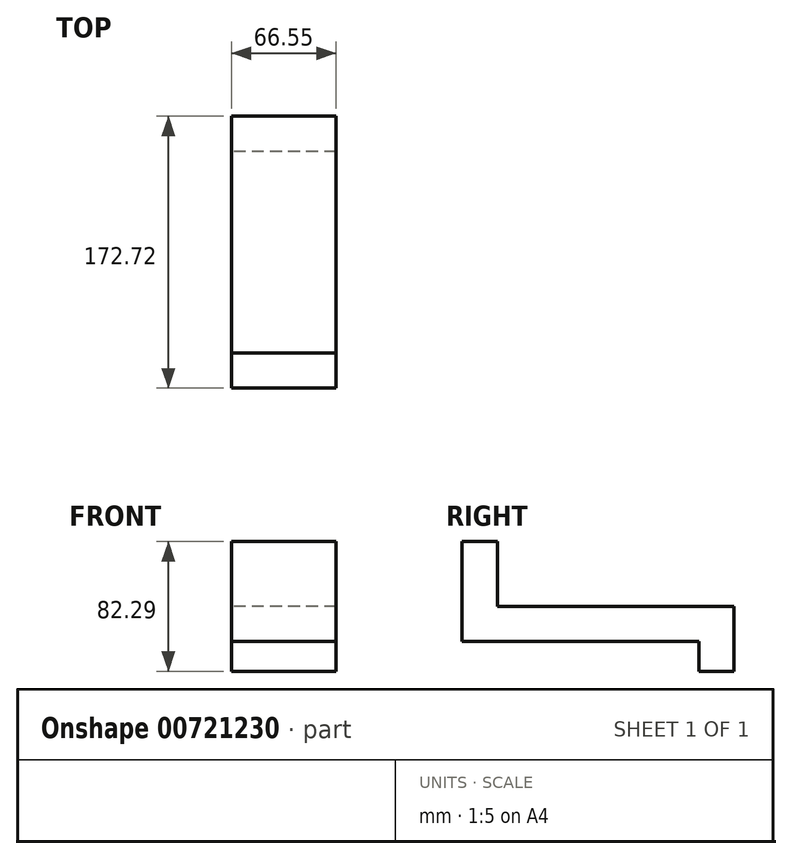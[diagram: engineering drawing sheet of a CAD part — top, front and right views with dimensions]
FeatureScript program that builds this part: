
annotation { "Feature Type Name" : "Feature", "Feature Type Description" : "" }
export const myFeature = defineFeature(function(context is Context, id is Id, definition is map)
    precondition{}
    {
        {
            var Q0;
            Q0=qCreatedBy(makeId("Right.planeOp"),FACE);
            var sketch = newSketch(context, id + "F0", { "sketchPlane" : qUnion([Q0])});
            skLineSegment(sketch, "E0", {"start": v(-54.94, 30.35) * mm, "end": v(-32.59, 30.35) * mm});
            skLineSegment(sketch, "E1", {"start": v(-32.59, 30.35) * mm, "end": v(-32.59, -10.8) * mm});
            skLineSegment(sketch, "E2", {"start": v(-32.59, -10.8) * mm, "end": v(117.78, -10.8) * mm});
            skLineSegment(sketch, "E3", {"start": v(117.78, -10.8) * mm, "end": v(117.78, -51.94) * mm});
            skLineSegment(sketch, "E4", {"start": v(117.78, -51.94) * mm, "end": v(95.43, -51.94) * mm});
            skLineSegment(sketch, "E5", {"start": v(95.43, -51.94) * mm, "end": v(95.43, -33.15) * mm});
            skLineSegment(sketch, "E6", {"start": v(95.43, -33.15) * mm, "end": v(-54.94, -33.15) * mm});
            skLineSegment(sketch, "E7", {"start": v(-54.94, -33.15) * mm, "end": v(-54.94, 30.35) * mm});
            skSolve(sketch);
        }
        {
            var Q0;
            Q0=makeQuery(id+"F0.imprint","IMPRINT",FACE,{"disambiguationData":[TD([[makeQuery(id+"F0.imprint","IMPRINT",EDGE,{"derivedFrom":sQuery(id+"F0.wireOp",EDGE,"E0")}),-1.0]])]});
            extrude(context, id + "F1", {"entities" : qUnion([Q0]), "depth" : 66.55 * mm, "offsetDistance" : 25.4 * mm});
        }
    });
